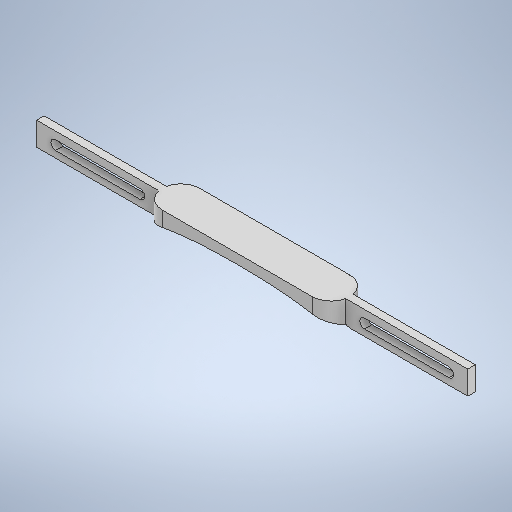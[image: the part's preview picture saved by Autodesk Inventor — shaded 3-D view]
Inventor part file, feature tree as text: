
AUTODESK INVENTOR PART (.ipt)
format: ipt  version: 2025.1 (Build 291241000, 241)  size: 320,512 bytes
history: native  units: in
note: dims shown in document units (in); Inventor stores cm internally (conversion verified against a paired STEP export)
features: sketch x3, extrude x3, move_body x3, fillet x2, direct_edit x2
ambient origin geometry x8: Origin, YZ Plane, XZ Plane, XY Plane, X Axis, Y Axis, Z Axis, Center Point
bodies: Solid1 (feature_tree)
feature tree (13):
  sketch  "Sketch1"  dims[d81=0.5in d82=0.0in d119=0.25in d135=0.25in]
  extrude  "Extrusion1"  Depth=0.25in
  fillet  "Fillet2"  Radius=0.25in
  direct_edit  "Direct Edit2"
  extrude  "Extrusion18"  Depth=0.1in TaperAngle=0.0deg
  fillet  "Fillet4"  Radius=0.8125in
  extrude  "Extrusion19"  Depth=0.125in
  direct_edit  "Direct Edit3"
  sketch  "Sketch6"  dims[d136=0.1in d140=0.0in d141=0.0in d142=1.0in]
  sketch  "Sketch7"  dims[d143=0.0in d144=0.0in d145=1.0in d146=0.8125in d147=0.0in d148=0.125in d158=0.8125in d159=0.0in d161=0.125in d162=0.25in d163=0.125in d164=0.0in d165=0.0in d166=-0.188in d27=0.5in d28=0.0344in d29=0.5in d30=0.0344in]
  move_body  "Move4"
  move_body  "Move5"
  move_body  "Move6"
